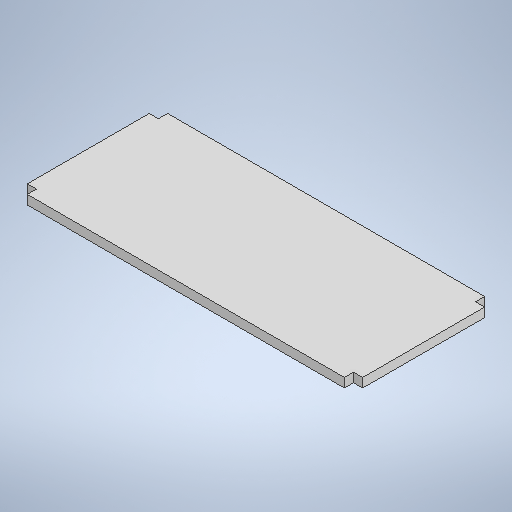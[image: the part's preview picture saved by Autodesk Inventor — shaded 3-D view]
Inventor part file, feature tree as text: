
AUTODESK INVENTOR PART (.ipt)
format: ipt  version: 2025 (Build 290162000, 162)  size: 251,904 bytes
history: native  units: in
note: dims shown in document units (in); Inventor stores cm internally (conversion verified against a paired STEP export)
features: extrude x3, sketch x3
ambient origin geometry x8: Origin, YZ Plane, XZ Plane, XY Plane, X Axis, Y Axis, Z Axis, Center Point
bodies: Solid1 (feature_tree)
feature tree (6):
  extrude  "Extrusion1"  Depth=18.1102in
  extrude  "Extrusion2"  Depth=1.1811in
  extrude  "Extrusion3"  Depth=1.1811in TaperAngle=0.0deg
  sketch  "Sketch1"  dims[d0=43.3071in d1=18.1102in]
  sketch  "Sketch2"  dims[d2=1.1811in d3=0.0in d6=1.1811in]
  sketch  "Sketch3"  dims[d7=1.1811in d8=1.1811in d9=0.0in d10=25.5906in d11=11.811in d12=1.1811in d13=0.0in]
